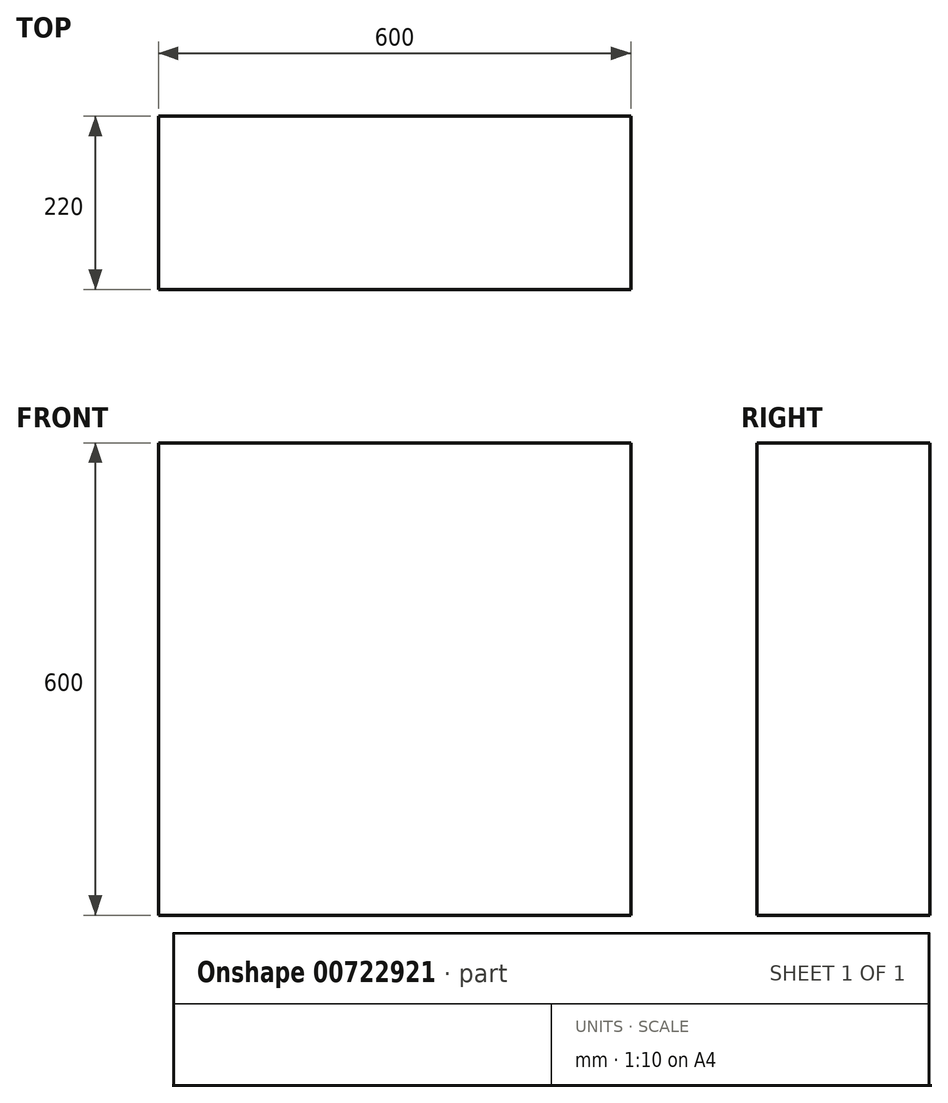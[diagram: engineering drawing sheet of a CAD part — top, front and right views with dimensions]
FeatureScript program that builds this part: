
annotation { "Feature Type Name" : "Feature", "Feature Type Description" : "" }
export const myFeature = defineFeature(function(context is Context, id is Id, definition is map)
    precondition{}
    {
        {
            var Q0;
            Q0=qCreatedBy(makeId("Front.planeOp"),FACE);
            var sketch = newSketch(context, id + "F0", { "sketchPlane" : qUnion([Q0])});
            skLineSegment(sketch, "E0.bottom", {"start": v(0, 0) * mm, "end": v(600, 0) * mm});
            skLineSegment(sketch, "E0.top", {"start": v(0, 600) * mm, "end": v(600, 600) * mm});
            skLineSegment(sketch, "E0.left", {"start": v(0, 0) * mm, "end": v(0, 600) * mm});
            skLineSegment(sketch, "E0.right", {"start": v(600, 0) * mm, "end": v(600, 600) * mm});
            skSolve(sketch);
        }
        {
            var Q0;
            Q0=makeQuery(id+"F0.imprint","IMPRINT",FACE,{"disambiguationData":[TD([[makeQuery(id+"F0.imprint","IMPRINT",EDGE,{"derivedFrom":sQuery(id+"F0.wireOp",EDGE,"E0.bottom")}),1.0]])]});
            extrude(context, id + "F1", {"entities" : qUnion([Q0]), "depth" : 220 * mm, "offsetDistance" : 25 * mm});
        }
    });
